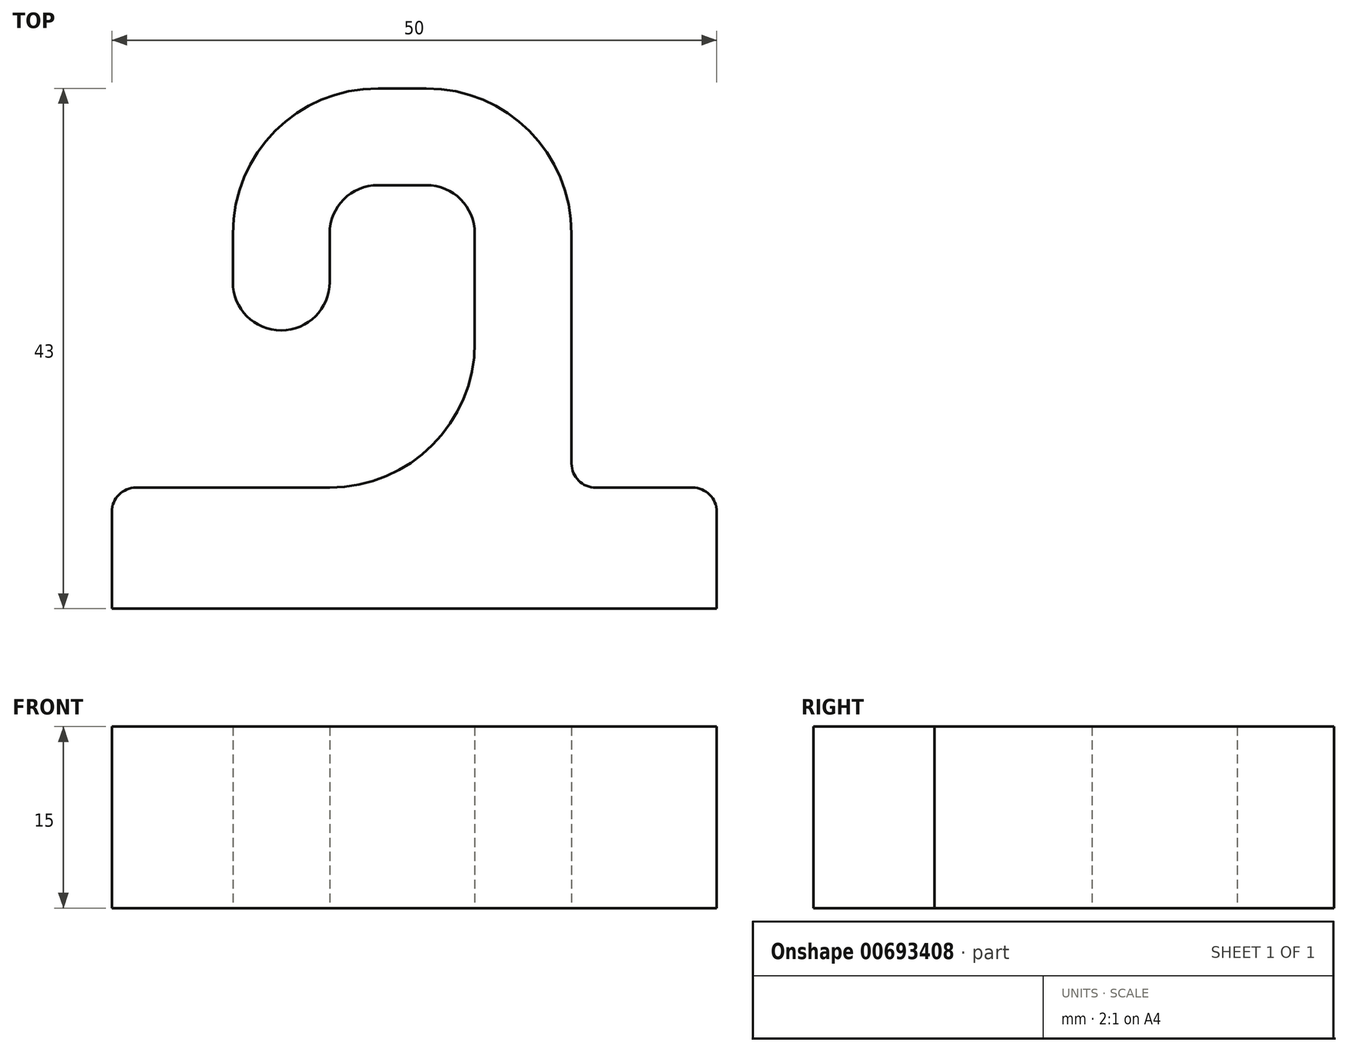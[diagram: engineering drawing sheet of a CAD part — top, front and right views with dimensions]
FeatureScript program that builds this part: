
annotation { "Feature Type Name" : "Feature", "Feature Type Description" : "" }
export const myFeature = defineFeature(function(context is Context, id is Id, definition is map)
    precondition{}
    {
        {
            var Q0;
            Q0=qCreatedBy(makeId("Top.planeOp"),FACE);
            var sketch = newSketch(context, id + "F0", { "sketchPlane" : qUnion([Q0])});
            skLineSegment(sketch, "E0.top", {"start": v(-28, 0) * mm, "end": v(22, 0) * mm});
            skLineSegment(sketch, "E0.left", {"start": v(-28, 8) * mm, "end": v(-28, 0) * mm});
            skLineSegment(sketch, "E0.right", {"start": v(22, 8) * mm, "end": v(22, 0) * mm});
            skLineSegment(sketch, "E1.top", {"start": v(0, 43) * mm, "end": v(-2, 43) * mm});
            skLineSegment(sketch, "E1.left", {"start": v(10, 12) * mm, "end": v(10, 31) * mm});
            skLineSegment(sketch, "E2.bottom", {"start": v(0, 43) * mm, "end": v(-3.05, 43) * mm});
            skLineSegment(sketch, "E2.top", {"start": v(-2, 35) * mm, "end": v(-6, 35) * mm});
            skLineSegment(sketch, "E3.bottom", {"start": v(-3.05, 43) * mm, "end": v(-6, 43) * mm});
            skLineSegment(sketch, "E3.top", {"start": v(-14, 23) * mm, "end": v(-14, 23) * mm});
            skLineSegment(sketch, "E3.right", {"start": v(-18, 31) * mm, "end": v(-18, 27) * mm});
            skPoint(sketch, "E4.visualSharp", {"position": v(-18, 23) * mm});
            skArc(sketch, "E4.filletArc", {"start": v(-18, 27) * mm, "mid": v(-16.83, 24.17) * mm, "end": v(-14, 23) * mm});
            skPoint(sketch, "E5.visualSharp", {"position": v(-9.05, 23) * mm});
            skArc(sketch, "E5.filletArc", {"start": v(-14, 23) * mm, "mid": v(-11.17, 24.17) * mm, "end": v(-10, 27) * mm});
            skPoint(sketch, "E6.visualSharp", {"position": v(-18, 43) * mm});
            skArc(sketch, "E6.filletArc", {"start": v(-6, 43) * mm, "mid": v(-14.49, 39.49) * mm, "end": v(-18, 31) * mm});
            skPoint(sketch, "E7.visualSharp", {"position": v(10, 43) * mm});
            skArc(sketch, "E7.filletArc", {"start": v(10, 31) * mm, "mid": v(6.49, 39.49) * mm, "end": v(-2, 43) * mm});
            skLineSegment(sketch, "E8", {"start": v(-10, 27) * mm, "end": v(-10, 31) * mm});
            skLineSegment(sketch, "E9", {"start": v(2, 31) * mm, "end": v(2, 22) * mm});
            skLineSegment(sketch, "E10", {"start": v(-26, 10) * mm, "end": v(-10, 10) * mm});
            skLineSegment(sketch, "E11", {"start": v(12, 10) * mm, "end": v(20, 10) * mm});
            skPoint(sketch, "E12.visualSharp", {"position": v(2, 35) * mm});
            skArc(sketch, "E12.filletArc", {"start": v(2, 31) * mm, "mid": v(0.83, 33.83) * mm, "end": v(-2, 35) * mm});
            skPoint(sketch, "E13.visualSharp", {"position": v(-10, 35) * mm});
            skArc(sketch, "E13.filletArc", {"start": v(-6, 35) * mm, "mid": v(-8.83, 33.83) * mm, "end": v(-10, 31) * mm});
            skPoint(sketch, "E14.visualSharp", {"position": v(10, 10) * mm});
            skArc(sketch, "E14.filletArc", {"start": v(10, 12) * mm, "mid": v(10.59, 10.59) * mm, "end": v(12, 10) * mm});
            skPoint(sketch, "E15.visualSharp", {"position": v(22, 10) * mm});
            skArc(sketch, "E15.filletArc", {"start": v(22, 8) * mm, "mid": v(21.41, 9.41) * mm, "end": v(20, 10) * mm});
            skPoint(sketch, "E16.visualSharp", {"position": v(-28, 10) * mm});
            skArc(sketch, "E16.filletArc", {"start": v(-26, 10) * mm, "mid": v(-27.41, 9.41) * mm, "end": v(-28, 8) * mm});
            skPoint(sketch, "E17.visualSharp", {"position": v(2, 10) * mm});
            skArc(sketch, "E17.filletArc", {"start": v(-10, 10) * mm, "mid": v(-1.51, 13.51) * mm, "end": v(2, 22) * mm});
            skSolve(sketch);
        }
        {
            var Q0;
            Q0=makeQuery(id+"F0.imprint","IMPRINT",FACE,{"disambiguationData":[TD([[makeQuery(id+"F0.imprint","IMPRINT",EDGE,{"derivedFrom":sQuery(id+"F0.wireOp",EDGE,"E0.top")}),1.0]])]});
            extrude(context, id + "F1", {"entities" : qUnion([Q0]), "depth" : 15 * mm, "offsetDistance" : 25 * mm});
        }
    });
